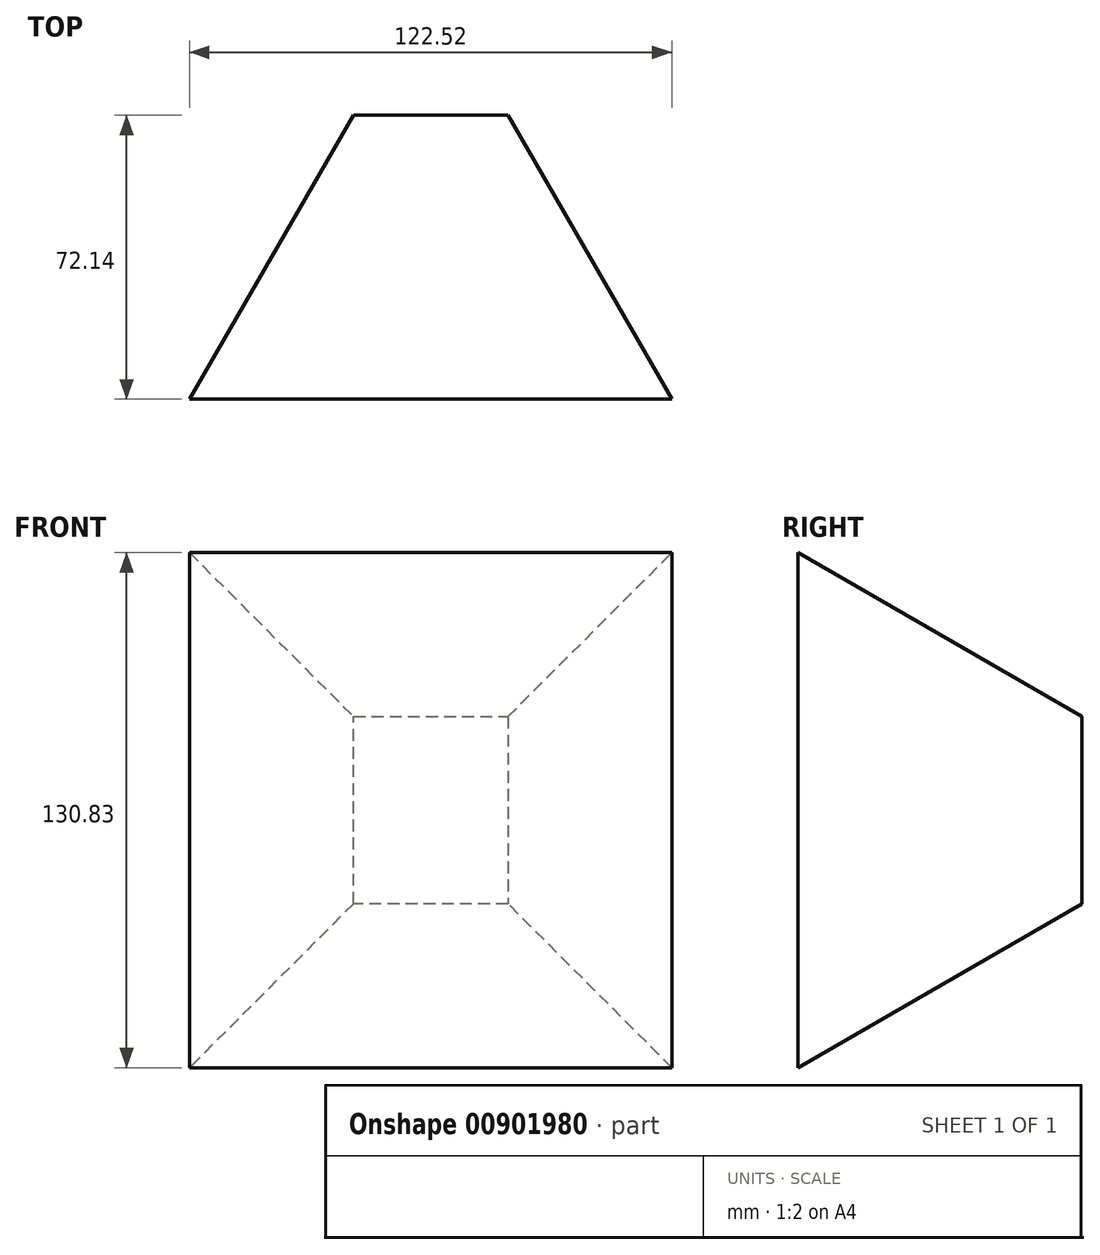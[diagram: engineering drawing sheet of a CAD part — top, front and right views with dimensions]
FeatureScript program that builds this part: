
annotation { "Feature Type Name" : "Feature", "Feature Type Description" : "" }
export const myFeature = defineFeature(function(context is Context, id is Id, definition is map)
    precondition{}
    {
        {
            var Q0;
            Q0=qCreatedBy(makeId("Front.planeOp"),FACE);
            var sketch = newSketch(context, id + "F0", { "sketchPlane" : qUnion([Q0])});
            skLineSegment(sketch, "E0.bottom", {"start": v(0, 0) * mm, "end": v(39.22, 0) * mm});
            skLineSegment(sketch, "E0.top", {"start": v(0, 47.54) * mm, "end": v(39.22, 47.54) * mm});
            skLineSegment(sketch, "E0.left", {"start": v(0, 0) * mm, "end": v(0, 47.54) * mm});
            skLineSegment(sketch, "E0.right", {"start": v(39.22, 0) * mm, "end": v(39.22, 47.54) * mm});
            skSolve(sketch);
        }
        {
            var Q0;
            Q0=makeQuery(id+"F0.imprint","IMPRINT",FACE,{"disambiguationData":[TD([[makeQuery(id+"F0.imprint","IMPRINT",EDGE,{"derivedFrom":sQuery(id+"F0.wireOp",EDGE,"E0.bottom")}),1.0]])]});
            extrude(context, id + "F1", {"entities" : qUnion([Q0]), "depth" : 72.14 * mm, "offsetDistance" : 25.4 * mm, "hasDraft" : true, "draftAngle" : 30 * degree});
        }
    });
